# Revit family: Plumbing_Valves_hansgrohe_26858707-FixFit-Wall-outlet-Porter-500-w_11
name_source: partatom
category: Plumbing Fixtures
revit_build: Autodesk Revit 2015 (Build: 20140903_1530(x64)
units: mm (PartAtom-declared; Revit-internal decimal feet)

## types (1)
- Matt White
    BIMobject category = Valves
    BIMobject category code = plumbing-valves
    BIMobject main category = Plumbing
    BIMobject main category code = plumbing
    BOSUseNativeGeometries = 1
    Brand url = http://www.hansgrohe-int.com
    Default Elevation = 4' - 0"
    Edition number = 1
    IFC Classification = Valve
    Installation instructions = https://pro.hansgrohe-int.com
    Manufacturer country = Germany
    Manufacturer name = hansgrohe
    Masterformat 2014 Code = 22 41 23
    Masterformat 2014 Description = Residential Showers
    NBS Reference Code = 94
    NBS Reference Description = Valves
    OmniClass Code = 23-31 11 19 11
    OmniClass Description = Thermostatically Controlled Faucet Mixing Valves
    Product Guid = 1b8319bc-dd69-4236-a95d-64022bf5cf6f
    Product SKU = 26858707
    Product data url = https://bimobject.com
    Product family = Fixfit
    Product group = Wall outlets
    Product name = 26858707 FixFit Wall outlet Porter 500 with shower holder and shower shelf R 26858707
    Product url = https://pro.hansgrohe-int.com
    QR code = http://bimobject.com
    Technical description = https://pro.hansgrohe-int.com
    UNSPSC Code = 40141616
    Uniclass 1.4 Code = L7117
    Uniclass 1.4 Description = Valves for water supply/distribution
    Uniclass 2.0 Code = PR-94
    Uniclass 2.0 Description = Valves
    Uniclass 2015 Code = Pr_65_54
    Uniclass 2015 Name = Valve products
    Uniformat II Code = D20
    Uniformat II Description = PLUMBING

## geometry (parser evidence)
native form markers: Sweep x3
no freeform markers — native parametric forms only
